# Revit family: Civil_Drainage_ACO_StormBrixx_Additional_Access_Chamber wm
name_source: partatom
category: Generic Models
revit_build: Autodesk Revit 2013 (Build: 20120221_2030(x64)
units: mm (PartAtom-declared; Revit-internal decimal feet)

## types (1)
- Civil_Drainage_ACO_StormBrixx_Additional_Access_Chamber wm
    Access Cover Dimensions = 528mm x 110mm (Diameter x Height)
    Access Cover Material = Ductile Iron
    Access Cover Product Code = 314056
    Access Cover Recyclable = Fully Recyclable
    Access Cover Recycled Material Content = Between 40% - 90%
    Access Cover Weight (kg) = 38
    Access Module Colour = Black
    Access Module Dimensions = 594mm x 594mm x 610mm (LxWxH)
    Access Module Material = High Density Polyethylene
    Access Module Product Code = 27034
    Access Module Recyclable = Fully Recyclable
    Access Module Recycled Material Content = 0%
    Access Module Weight (kg) = 32
    Assembly Code = D2090300
    Cost = 0 $
    Current Revision = 1
    Depth = 110 mm
    Description = Access Chamber Module
    Distributed by = www.aco.co.uk
    Fax = +44 (0)1462 815895
    Installation Guidelines = http://www.aco.co.uk
    Keynote = R17:315
    Length = 600 mm
    Maintenance Guidelines = http://www.aco.co.uk
    Manufacturer = ACO Technologies plc
    Model = StormBrixx accessories
    Product Range = ACO StormBrixx
    Product Type = Stormwater attenuation & infiltration
    Product Website = www.stormbrixx.co.uk
    Telephone = +44 (0)1462 816666
    Type Comments = Access Chamber Module
    URL = www.aco.co.uk
    pipe fitting = Generic Plastic Pipe

## geometry (parser evidence)
native form markers: Blend x4, Sweep x3
no freeform markers — native parametric forms only
